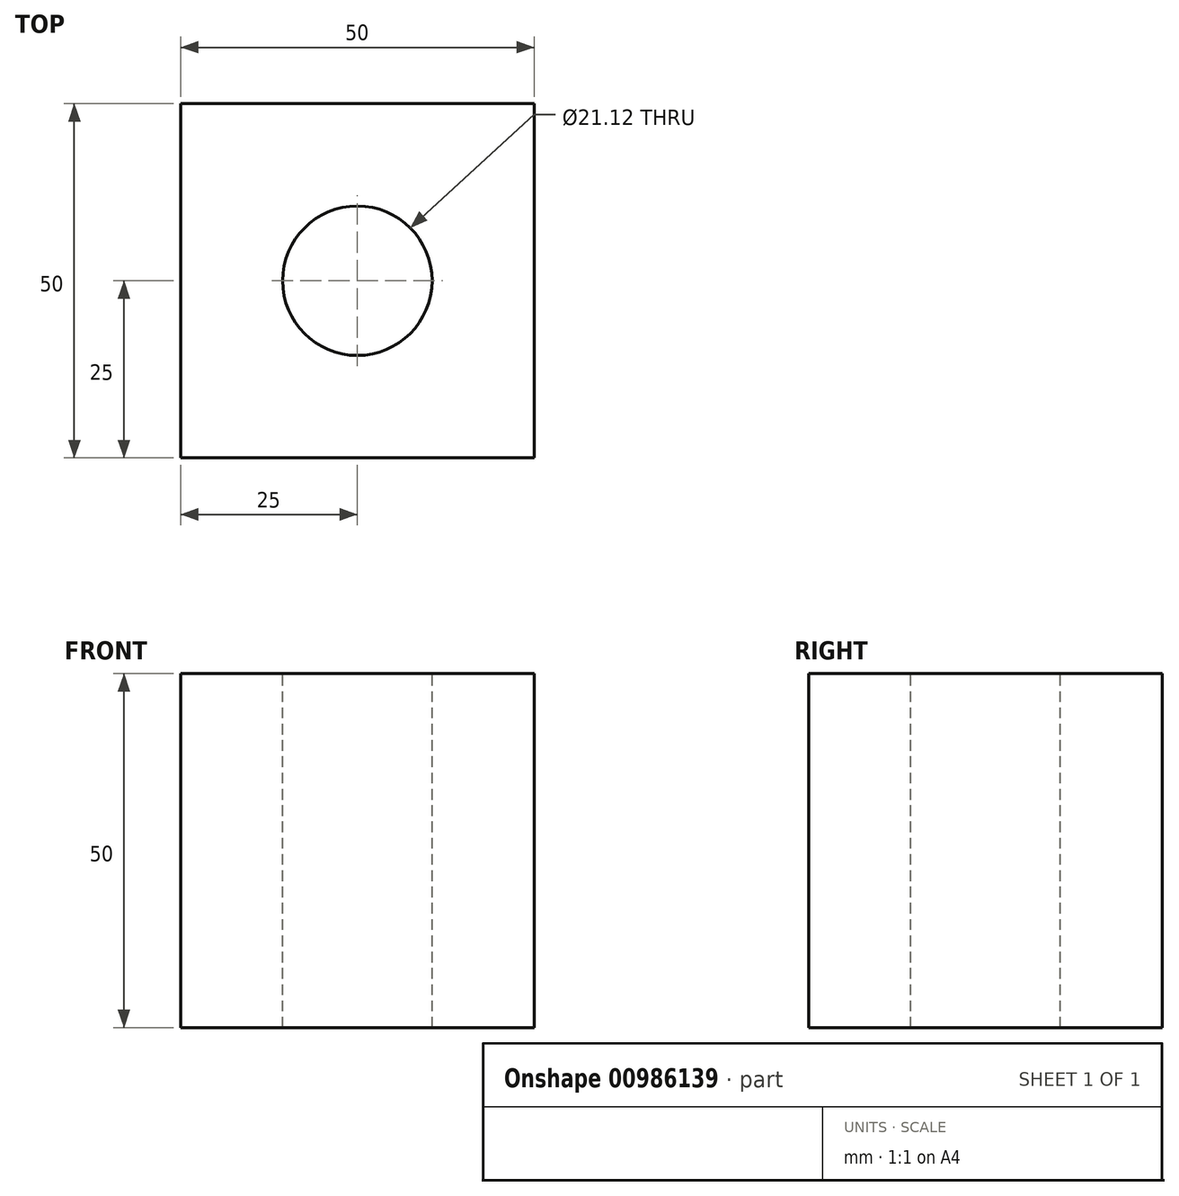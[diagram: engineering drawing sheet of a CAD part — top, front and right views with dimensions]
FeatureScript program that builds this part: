
annotation { "Feature Type Name" : "Feature", "Feature Type Description" : "" }
export const myFeature = defineFeature(function(context is Context, id is Id, definition is map)
    precondition{}
    {
        {
            var Q0;
            Q0=qCreatedBy(makeId("Top.planeOp"),FACE);
            var sketch = newSketch(context, id + "F0", { "sketchPlane" : qUnion([Q0])});
            skLineSegment(sketch, "E0.bottom", {"start": v(25, -25) * mm, "end": v(-25, -25) * mm});
            skLineSegment(sketch, "E0.top", {"start": v(25, 25) * mm, "end": v(-25, 25) * mm});
            skLineSegment(sketch, "E0.left", {"start": v(25, -25) * mm, "end": v(25, 25) * mm});
            skLineSegment(sketch, "E0.right", {"start": v(-25, -25) * mm, "end": v(-25, 25) * mm});
            skPoint(sketch, "E0.middle", {"position": v(0, 0) * mm});
            skSolve(sketch);
        }
        {
            var Q0;
            Q0=makeQuery(id+"F0.imprint","IMPRINT",FACE,{"disambiguationData":[TD([[makeQuery(id+"F0.imprint","IMPRINT",EDGE,{"derivedFrom":sQuery(id+"F0.wireOp",EDGE,"E0.bottom")}),-1.0]])]});
            extrude(context, id + "F1", {"entities" : qUnion([Q0]), "oppositeDirection" : true, "depth" : 50 * mm, "offsetDistance" : 25.4 * mm});
        }
        {
            var Q0;
            Q0=makeQuery(id+"F1.opExtrude","CAP_FACE",FACE,{"disambiguationData":[OSD([sQuery(id+"F0.wireOp",EDGE,"E0.bottom"),sQuery(id+"F0.wireOp",EDGE,"E0.top"),sQuery(id+"F0.wireOp",EDGE,"E0.left"),sQuery(id+"F0.wireOp",EDGE,"E0.right")])],"isStart":true});
            var sketch = newSketch(context, id + "F2", { "sketchPlane" : qUnion([Q0])});
            skSolve(sketch);
        }
        {
            var Q0;
            Q0=makeQuery(id+"F2.imprint","IMPRINT",FACE,{"disambiguationData":[TD([[makeQuery(id+"F2.imprint","IMPRINT",EDGE,{"derivedFrom":makeQuery(id+"F1.opExtrude","CAP_EDGE",EDGE,{"disambiguationData":[OSD([sQuery(id+"F0.wireOp",EDGE,"E0.bottom")])],"isStart":true})}),-1.0]])]});
            var sketch = newSketch(context, id + "F3", { "sketchPlane" : qUnion([Q0])});
            skCircle(sketch, "E1", {"center": v(0, 0) * mm, "radius": 10.56 * mm});
            skSolve(sketch);
        }
        {
            var Q0;
            Q0=makeQuery(id+"F3.imprint","IMPRINT",FACE,{"disambiguationData":[TD([[makeQuery(id+"F3.imprint","IMPRINT",EDGE,{"derivedFrom":sQuery(id+"F3.wireOp",EDGE,"E1")}),1.0]])]});
            var Q1;
            Q1=sQuery(id+"F3.wireOp",EDGE,"E1");
            extrude(context, id + "F4", {"entities" : qUnion([Q0]), "operationType" : NewBodyOperationType.REMOVE, "surfaceEntities" : qUnion([Q1]), "oppositeDirection" : true, "depth" : 150 * mm, "offsetDistance" : 25 * mm});
        }
    });
